annotation { "Feature Type Name" : "Feature", "Feature Type Description" : "" }
export const myFeature = defineFeature(function(context is Context, id is Id, definition is map)
    precondition{}
    {
        {
            var Q0;
            Q0=qCreatedBy(makeId("Top.planeOp"),FACE);
            var sketch = newSketch(context, id + "F0", { "sketchPlane" : qUnion([Q0])});
            skLineSegment(sketch, "E0.bottom", {"start": v(0, 0) * mm, "end": v(-154, 0) * mm});
            skLineSegment(sketch, "E0.top", {"start": v(0, 46) * mm, "end": v(-154, 46) * mm});
            skLineSegment(sketch, "E0.left", {"start": v(0, 0) * mm, "end": v(0, 46) * mm});
            skLineSegment(sketch, "E0.right", {"start": v(-154, 0) * mm, "end": v(-154, 46) * mm});
            skLineSegment(sketch, "E1.bottom", {"start": v(-144, 36) * mm, "end": v(-118, 36) * mm});
            skLineSegment(sketch, "E1.top", {"start": v(-144, 10) * mm, "end": v(-118, 10) * mm});
            skLineSegment(sketch, "E1.left", {"start": v(-144, 36) * mm, "end": v(-144, 10) * mm});
            skLineSegment(sketch, "E1.right", {"start": v(-118, 36) * mm, "end": v(-118, 10) * mm});
            skLineSegment(sketch, "E2.bottom", {"start": v(-108, 36) * mm, "end": v(-82, 36) * mm});
            skLineSegment(sketch, "E2.top", {"start": v(-108, 10) * mm, "end": v(-82, 10) * mm});
            skLineSegment(sketch, "E2.left", {"start": v(-108, 36) * mm, "end": v(-108, 10) * mm});
            skLineSegment(sketch, "E2.right", {"start": v(-82, 36) * mm, "end": v(-82, 10) * mm});
            skLineSegment(sketch, "E3.bottom", {"start": v(-72, 36) * mm, "end": v(-46, 36) * mm});
            skLineSegment(sketch, "E3.top", {"start": v(-72, 10) * mm, "end": v(-46, 10) * mm});
            skLineSegment(sketch, "E3.left", {"start": v(-72, 36) * mm, "end": v(-72, 10) * mm});
            skLineSegment(sketch, "E3.right", {"start": v(-46, 36) * mm, "end": v(-46, 10) * mm});
            skLineSegment(sketch, "E4.bottom", {"start": v(-36, 36) * mm, "end": v(-10, 36) * mm});
            skLineSegment(sketch, "E4.top", {"start": v(-36, 10) * mm, "end": v(-10, 10) * mm});
            skLineSegment(sketch, "E4.left", {"start": v(-36, 36) * mm, "end": v(-36, 10) * mm});
            skLineSegment(sketch, "E4.right", {"start": v(-10, 36) * mm, "end": v(-10, 10) * mm});
            skSolve(sketch);
        }
        {
            var Q0;
            Q0 = qSketchRegion(id + "F0", true);
            var Q1;
            Q1=makeQuery(id+"F0.imprint","IMPRINT",FACE,{"disambiguationData":[TD([[makeQuery(id+"F0.imprint","IMPRINT",EDGE,{"derivedFrom":sQuery(id+"F0.wireOp",EDGE,"E1.bottom")}),-1.0]])]});
            var Q2;
            Q2=makeQuery(id+"F0.imprint","IMPRINT",FACE,{"disambiguationData":[TD([[makeQuery(id+"F0.imprint","IMPRINT",EDGE,{"derivedFrom":sQuery(id+"F0.wireOp",EDGE,"E2.bottom")}),-1.0]])]});
            var Q3;
            Q3=makeQuery(id+"F0.imprint","IMPRINT",FACE,{"disambiguationData":[TD([[makeQuery(id+"F0.imprint","IMPRINT",EDGE,{"derivedFrom":sQuery(id+"F0.wireOp",EDGE,"E3.bottom")}),-1.0]])]});
            var Q4;
            Q4=makeQuery(id+"F0.imprint","IMPRINT",FACE,{"disambiguationData":[TD([[makeQuery(id+"F0.imprint","IMPRINT",EDGE,{"derivedFrom":sQuery(id+"F0.wireOp",EDGE,"E4.bottom")}),-1.0]])]});
            extrude(context, id + "F1", {"entities" : qUnion([Q0, Q1, Q2, Q3, Q4]), "oppositeDirection" : true, "depth" : 19 * mm});
        }
        {
            var Q0;
            Q0=makeQuery(id+"F0.imprint","IMPRINT",FACE,{"disambiguationData":[TD([[makeQuery(id+"F0.imprint","IMPRINT",EDGE,{"derivedFrom":sQuery(id+"F0.wireOp",EDGE,"E1.bottom")}),-1.0]])]});
            var Q1;
            Q1=makeQuery(id+"F0.imprint","IMPRINT",FACE,{"disambiguationData":[TD([[makeQuery(id+"F0.imprint","IMPRINT",EDGE,{"derivedFrom":sQuery(id+"F0.wireOp",EDGE,"E2.bottom")}),-1.0]])]});
            var Q2;
            Q2=makeQuery(id+"F0.imprint","IMPRINT",FACE,{"disambiguationData":[TD([[makeQuery(id+"F0.imprint","IMPRINT",EDGE,{"derivedFrom":sQuery(id+"F0.wireOp",EDGE,"E3.bottom")}),-1.0]])]});
            var Q3;
            Q3=makeQuery(id+"F0.imprint","IMPRINT",FACE,{"disambiguationData":[TD([[makeQuery(id+"F0.imprint","IMPRINT",EDGE,{"derivedFrom":sQuery(id+"F0.wireOp",EDGE,"E4.bottom")}),-1.0]])]});
            extrude(context, id + "F2", {"entities" : qUnion([Q0, Q1, Q2, Q3]), "operationType" : NewBodyOperationType.REMOVE, "oppositeDirection" : true, "depth" : 17 * mm});
        }
        {
            var Q0;
            Q0=makeQuery(id+"F0.imprint","IMPRINT",FACE,{"disambiguationData":[TD([[makeQuery(id+"F0.imprint","IMPRINT",EDGE,{"derivedFrom":sQuery(id+"F0.wireOp",EDGE,"E0.bottom")}),-1.0]])]});
            var sketch = newSketch(context, id + "F3", { "sketchPlane" : qUnion([Q0])});
            skText(sketch, "E5", { "text": "Infill Density", "fontName": "OpenSans-Regular.ttf"});
            skText(sketch, "E6", { "text": "5%", "fontName": "OpenSans-Regular.ttf"});
            skText(sketch, "E7", { "text": "25%", "fontName": "OpenSans-Regular.ttf"});
            skText(sketch, "E8", { "text": "50%", "fontName": "OpenSans-Regular.ttf"});
            skText(sketch, "E9", { "text": "75%", "fontName": "OpenSans-Regular.ttf"});
            const initialGuessF3  = {"E5": [-0.09968, 0.03891, 1, 0, 0.00598], "E6": [-0.138, 0.00184, 1, 0, 0.007], "E7": [-0.10402, 0.00198, 1, 0, 0.007], "E8": [-0.06774, 0.00184, 1, 0, 0.007], "E9": [-0.03257, 0.00156, 1, 0, 0.007]};
            skSetInitialGuess(sketch, initialGuessF3);
            skSolve(sketch);
        }
        {
            var Q0;
            Q0 = qSketchRegion(id + "F3", true);
            extrude(context, id + "F4", {"entities" : qUnion([Q0]), "operationType" : NewBodyOperationType.ADD, "depth" : 1.6 * mm});
        }
    });